# Revit family: Считыватель AGRG AXI 3_тип модель
name_source: partatom
category: Охранная сигнализация
units: mm (PartAtom-declared; Revit-internal decimal feet)

## family parameters
Всегда вертикально = Да
На основе рабочей плоскости = Нет
Общий = Нет
При загрузке вырезать с полостями = Нет
Размер круглого соединителя = Использовать диаметр
Сохранять ориентацию аннотаций = Нет
Тип детали = Нормальный
Точка расчета площади = Нет

## types (3) — shared parameters
ADSK_Верхний порог напряжения = 15 В
ADSK_Группирование = 1. Оборудование
ADSK_Единица измерения = шт.
ADSK_Завод-изготовитель = ООО «Агрегатор»
ADSK_Количество = 1
ADSK_Марка = AGRG AXI
ADSK_Масса = 0.06
ADSK_Наименование краткое = Считыватель бесконтактных карт
ADSK_Нижний порог напряжения = 9 В
ADSK_Обозначение = RC
ITV_SUB_УГО на структурной схеме = УГО_Считыватель
LT = InformationFamily
URL = https://skud.agrg.ru
Изображение типоразмера = RC.png
Описание = ITV
Стоимость = 14250 $

## per-type parameters (varying)
| type | ADSK_Код изделия | ADSK_Наименование | Материал |
| Считыватель AGRG AXI 3 «Арктический белый» | AXI3AW | Считыватель для СКУД AGRG AXI 3. Совместим с БОЛИД. "Арктический белый" | Пластмасса, непрозрачная, белая |
| Считыватель AGRG AXI 3 «Люксовый Мандарин» | AXI3LM | Считыватель для СКУД AGRG AXI 3. Совместим с БОЛИД. "Люксовый мандарин" | Пластмасса, непрозрачная, оранжевая |
| Считыватель AGRG AXI 3 «Имперский черный» | AXI3IBL | Считыватель для СКУД AGRG AXI 3. Совместим с БОЛИД. "Имперский черный" | Пластмасса, непрозрачная, черная |
